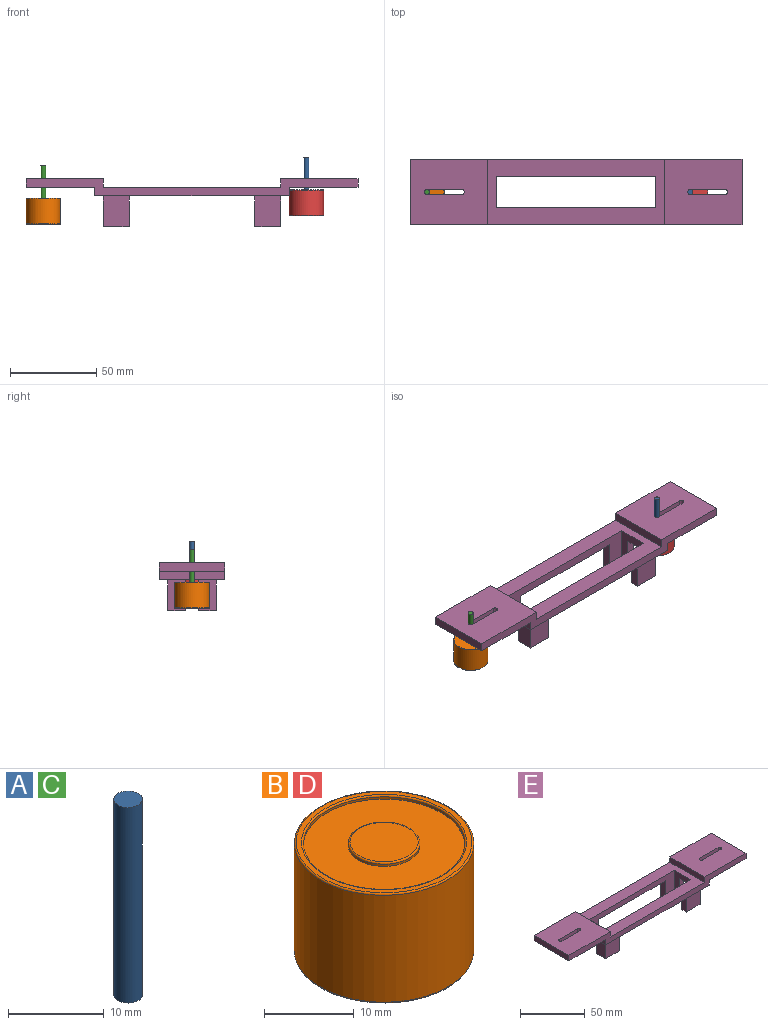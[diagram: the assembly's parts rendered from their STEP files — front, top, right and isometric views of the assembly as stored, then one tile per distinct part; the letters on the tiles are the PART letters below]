
ASSEMBLY  parts=5 mates=4
PART A: 3 faces, bbox 3x3x25 mm
  f0: cylinder r=1.5mm len=25mm, axis (0,0,-1), area 235.6mm2, adj f1,f2
  f1: plane 3x3mm, normal (0,0,1), area 7.1mm2, adj f0
  f2: plane 3x3mm, normal (0,0,-1), area 7.1mm2, adj f0
PART B: 13 faces, bbox 21.6x21.6x15 mm
  f0: cylinder r=9mm len=18mm, axis (0,0,-1), area 17mm2, adj f6,f12
  f1: cylinder r=10mm len=20mm, axis (0,0,-1), area 917.3mm2, adj f4,f5
  f2: plane 19.6x19.6mm, normal (0,0,1), area 35.8mm2, adj f5,f12
  f3: plane 19.6x19.6mm, normal (0,0,-1), area 294.6mm2, adj f4,f7
  f4: torus R=9.8mm, axis (0,0,1), area 19.6mm2, adj f1,f3
  f5: torus R=9.8mm, axis (0,0,1), area 19.6mm2, adj f1,f2
  f6: plane 18x18mm, normal (0,0,1), area 204.2mm2, adj f0,f9
  f7: cylinder r=1.5mm len=6mm, axis (0,0,-1), area 56.5mm2, adj f3,f8
  f8: plane 3x3mm, normal (0,0,-1), area 7.1mm2, adj f7
  f9: cylinder r=4mm len=8mm, axis (0,0,-1), area 7.5mm2, adj f6,f11
  f10: plane 7.6x7.6mm, normal (0,0,1), area 45.4mm2, adj f11
  f11: torus R=3.8mm, axis (0,0,1), area 7.8mm2, adj f9,f10
  f12: torus R=9.2mm, axis (0,0,1), area 17.9mm2, adj f0,f2
PART C: same geometry as A
PART D: same geometry as B
PART E: 46 faces, bbox 193x38x28 mm
  f0: plane 18x10mm, normal (1,0,0), area 180mm2, adj f1,f5,f19,f42
  f1: plane 18x15mm, normal (0,1,0), area 270mm2, adj f0,f5,f19,f44
  f2: plane 18x10mm, normal (-1,0,0), area 180mm2, adj f6,f16,f19,f38
  f3: plane 18x15mm, normal (0,-1,0), area 270mm2, adj f7,f15,f19,f40
  f4: plane 15x10mm, normal (0,0,-1), area 100mm2, adj f9,f14,f17,f18,f39,f41
  f5: plane 15x10mm, normal (0,0,-1), area 100mm2, adj f0,f1,f8,f13,f42,f44
  f6: plane 15x10mm, normal (0,0,-1), area 100mm2, adj f2,f8,f9,f16,f38,f45
  f7: plane 15x10mm, normal (0,0,-1), area 100mm2, adj f3,f13,f14,f15,f40,f43
  f8: plane 93x23mm, normal (0,-1,0), area 825mm2, adj f5,f6,f9,f13,f19,f23,f44,f45
  f9: plane 23x18mm, normal (1,0,0), area 270mm2, adj f4,f6,f8,f14,f19,f23,f38,f39
  f10: plane 45x38mm, normal (0,0,1), area 1642.9mm2, adj f20,f21,f24,f29,f30,f31,f32,f33
  f11: plane 40x38mm, normal (0,0,-1), area 1452.9mm2, adj f12,f20,f21,f29,f30,f31,f32,f33
  f12: plane 38x5mm, normal (-1,0,0), area 190mm2, adj f11,f19,f20,f21
  f13: plane 23x18mm, normal (-1,0,0), area 270mm2, adj f5,f7,f8,f14,f19,f23,f42,f43
  f14: plane 93x23mm, normal (0,1,0), area 825mm2, adj f4,f7,f9,f13,f19,f23,f40,f41
  f15: plane 18x10mm, normal (1,0,0), area 180mm2, adj f3,f7,f19,f43
  f16: plane 18x15mm, normal (0,1,0), area 270mm2, adj f2,f6,f19,f45
  f17: plane 18x10mm, normal (-1,0,0), area 180mm2, adj f4,f18,f19,f39
  f18: plane 18x15mm, normal (0,-1,0), area 270mm2, adj f4,f17,f19,f41
  f19: plane 113x38mm, normal (0,0,-1), area 2220mm2, adj f0,f1,f2,f3,f8,f9,f12,f13
  f20: plane 193x10mm, normal (0,1,0), area 1015mm2, adj f10,f11,f12,f19,f22,f23,f24,f25
  f21: plane 193x10mm, normal (0,-1,0), area 1015mm2, adj f10,f11,f12,f19,f22,f23,f24,f25
  f22: plane 38x5mm, normal (1,0,0), area 190mm2, adj f19,f20,f21,f27
  f23: plane 103x38mm, normal (0,0,1), area 2240mm2, adj f8,f9,f13,f14,f20,f21,f24,f25
  f24: plane 38x5mm, normal (1,0,0), area 190mm2, adj f10,f20,f21,f23
  f25: plane 38x5mm, normal (-1,0,0), area 190mm2, adj f20,f21,f23,f26
  f26: plane 45x38mm, normal (0,0,1), area 1642.9mm2, adj f20,f21,f25,f28,f34,f35,f36,f37
  f27: plane 40x38mm, normal (0,0,-1), area 1452.9mm2, adj f20,f21,f22,f28,f34,f35,f36,f37
  f28: plane 38x5mm, normal (1,0,0), area 190mm2, adj f20,f21,f26,f27
  f29: plane 38x5mm, normal (-1,0,0), area 190mm2, adj f10,f11,f20,f21
  f30: plane 20x5mm, normal (0,1,0), area 100mm2, adj f10,f11,f31,f33
  f31: cylinder r=1.5mm len=5mm, axis (0,0,-1), area 23.6mm2, adj f10,f11,f30,f32
  f32: plane 20x5mm, normal (0,-1,0), area 100mm2, adj f10,f11,f31,f33
  f33: cylinder r=1.5mm len=5mm, axis (0,0,-1), area 23.6mm2, adj f10,f11,f30,f32
  f34: plane 20x5mm, normal (0,-1,0), area 100mm2, adj f26,f27,f35,f37
  f35: cylinder r=1.5mm len=5mm, axis (0,0,-1), area 23.6mm2, adj f26,f27,f34,f36
  f36: plane 20x5mm, normal (0,1,0), area 100mm2, adj f26,f27,f35,f37
  f37: cylinder r=1.5mm len=5mm, axis (0,0,-1), area 23.6mm2, adj f26,f27,f34,f36
  f38: plane 18x5mm, normal (0,-1,0), area 90mm2, adj f2,f6,f9,f19
  f39: plane 18x5mm, normal (0,1,0), area 90mm2, adj f4,f9,f17,f19
  f40: plane 18x5mm, normal (-1,0,0), area 90mm2, adj f3,f7,f14,f19
  f41: plane 18x5mm, normal (1,0,0), area 90mm2, adj f4,f14,f18,f19
  f42: plane 18x5mm, normal (0,-1,0), area 90mm2, adj f0,f5,f13,f19
  f43: plane 18x5mm, normal (0,1,0), area 90mm2, adj f7,f13,f15,f19
  f44: plane 18x5mm, normal (-1,0,0), area 90mm2, adj f1,f5,f8,f19
  f45: plane 18x5mm, normal (1,0,0), area 90mm2, adj f6,f8,f16,f19
PLACE A t=(66.5,0,15.5)mm
PLACE B rot(axis=(1,0,0),180deg) t=(-86.5,0,16.5)mm
PLACE C rot(axis=(1,0,0),180deg) t=(-86.5,0,35.5)mm
PLACE D rot(axis=(1,0,0),180deg) t=(66.5,0,21.5)mm
PLACE E at identity
MATE fastened B.f7 <-> C.f0  axis (0,0,1) through (-86.5,0,10.5)mm
MATE fastened D.f7 <-> A.f0  axis (0,0,1) through (66.5,0,15.5)mm
MATE pin_slot C.f0 <-> E.f11  axis (0,0,1) through (-86.5,0,23)mm
MATE pin_slot E.f26 <-> A.f0  axis (0,0,1) through (76.5,0,28)mm
